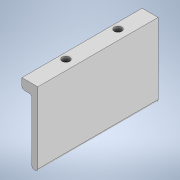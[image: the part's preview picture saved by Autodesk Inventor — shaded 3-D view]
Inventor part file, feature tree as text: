
AUTODESK INVENTOR PART (.ipt)
format: ipt  version: 2020 (Build 240168000, 168)  size: 203,264 bytes
history: native  units: mm
features: extrude x7, sketch x7, fillet x1
ambient origin geometry x8: Origin, YZ Plane, XZ Plane, XY Plane, X Axis, Y Axis, Z Axis, Center Point
bodies: Solid1 (feature_tree)
feature tree (15):
  extrude  "Extrusion1"  Depth=30.0mm
  extrude  "Extrusion7"  Depth=1.5mm TaperAngle=0.0deg
  extrude  "Extrusion8"  Depth=3.1mm
  extrude  "Extrusion9"  Depth=21.2mm
  extrude  "Extrusion10"  Depth=2.0mm
  fillet  "Fillet1"  Radius=2.0mm
  extrude  "Extrusion13"  Depth=4.0mm
  extrude  "Extrusion14"  Depth=4.0mm
  sketch  "Sketch1"  dims[d0=8.0mm d1=30.0mm]
  sketch  "Sketch8"  dims[d2=60.0mm d3=0.0mm d42=1.5mm d43=0.0mm]
  sketch  "Sketch9"  dims[d44=3.1mm d45=3.1mm]
  sketch  "Sketch11"  dims[d46=21.2mm d47=2.5mm]
  sketch  "Sketch12"  dims[d48=2.5mm d49=17.85mm d53=2.0mm d54=0.0mm]
  sketch  "Sketch15"  dims[d55=4.0mm d56=4.0mm]
  sketch  "Sketch16"  dims[d57=4.0mm d58=4.0mm d59=2.0mm d60=0.0mm d64=0.0mm d65=0.0mm d66=1.0mm d71=4.05mm d72=4.0mm d73=5.5mm d74=0.0mm d75=5.5mm d76=0.0mm d22=0.5mm d23=0.872665mm d24=0.5mm d25=0.872665mm]
